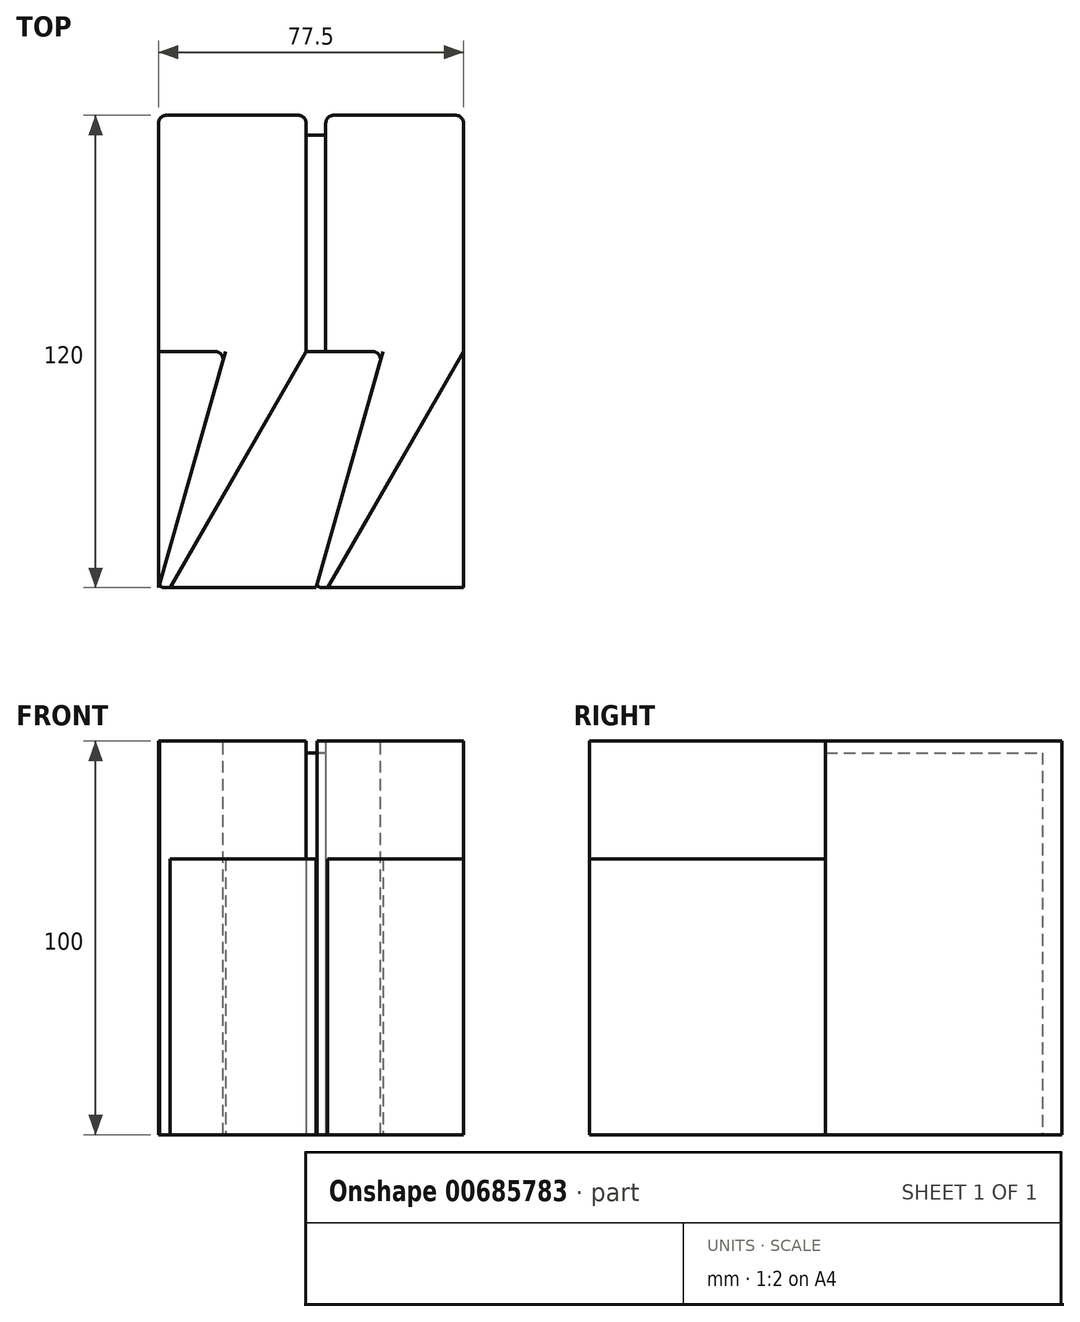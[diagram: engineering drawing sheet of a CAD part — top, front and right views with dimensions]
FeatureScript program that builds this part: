
annotation { "Feature Type Name" : "Feature", "Feature Type Description" : "" }
export const myFeature = defineFeature(function(context is Context, id is Id, definition is map)
    precondition{}
    {
        {
            var Q0;
            Q0=qCreatedBy(makeId("Top.planeOp"),FACE);
            var sketch = newSketch(context, id + "F0", { "sketchPlane" : qUnion([Q0])});
            skLineSegment(sketch, "E0.bottom", {"start": v(37.5, 60) * mm, "end": v(-40, 60) * mm});
            skLineSegment(sketch, "E0.top", {"start": v(37.5, -60) * mm, "end": v(-40, -60) * mm});
            skLineSegment(sketch, "E0.right", {"start": v(-40, 60) * mm, "end": v(-40, -60) * mm});
            skPoint(sketch, "E0.middle", {"position": v(0, 0) * mm});
            skLineSegment(sketch, "E1", {"start": v(-40, 0) * mm, "end": v(-23, 0) * mm});
            skLineSegment(sketch, "E2", {"start": v(-23, 0) * mm, "end": v(-40, -60) * mm});
            skLineSegment(sketch, "E3", {"start": v(17, 0) * mm, "end": v(0, -60) * mm});
            skLineSegment(sketch, "E4", {"start": v(0, -60) * mm, "end": v(3, -60) * mm});
            skLineSegment(sketch, "E5", {"start": v(3, -60) * mm, "end": v(0, -60) * mm});
            skLineSegment(sketch, "E6", {"start": v(-37, -60) * mm, "end": v(-40, -60) * mm});
            skPoint(sketch, "E7.end.orphan", {"position": v(30.1, 0) * mm});
            skPoint(sketch, "E8.start.orphan", {"position": v(-9.9, 0) * mm});
            skLineSegment(sketch, "E9", {"start": v(-37, -60) * mm, "end": v(-2.5, 0) * mm});
            skLineSegment(sketch, "E10", {"start": v(3, -60) * mm, "end": v(37.5, 0) * mm});
            skLineSegment(sketch, "E11", {"start": v(37.5, 0) * mm, "end": v(37.5, 60) * mm});
            skLineSegment(sketch, "E12", {"start": v(37.5, 0) * mm, "end": v(37.5, -60) * mm});
            skPoint(sketch, "E0.left.start.orphan", {"position": v(40, 60) * mm});
            skPoint(sketch, "E13.orphan", {"position": v(40, -60) * mm});
            skLineSegment(sketch, "E14", {"start": v(-2.5, 0) * mm, "end": v(17, 0) * mm});
            skLineSegment(sketch, "E15", {"start": v(-2.5, 0) * mm, "end": v(-2.5, 60) * mm});
            skLineSegment(sketch, "E16", {"start": v(2.5, 0) * mm, "end": v(2.5, 60) * mm});
            skSolve(sketch);
        }
        {
            var Q0;
            {var subQ3=sQuery(id+"F0.wireOp",EDGE,"E1");Q0=makeQuery(id+"F0.imprint","IMPRINT",FACE,{"disambiguationData":[TD([[makeQuery(id+"F0.imprint","IMPRINT",EDGE,{"derivedFrom":subQ3}),1.0]])]});}
            var Q1;
            {var subQ0=sQuery(id+"F0.wireOp",EDGE,"E3");Q1=makeQuery(id+"F0.imprint","IMPRINT",FACE,{"disambiguationData":[TD([[makeQuery(id+"F0.imprint","IMPRINT",EDGE,{"derivedFrom":subQ0}),1.0]])]});}
            extrude(context, id + "F1", {"entities" : qUnion([Q0, Q1]), "depth" : 100 * mm, "offsetDistance" : 25 * mm});
        }
        {
            var Q0;
            {var subQ2=sQuery(id+"F0.wireOp",EDGE,"E1");Q0=makeQuery(id+"F0.imprint","IMPRINT",FACE,{"disambiguationData":[TD([[makeQuery(id+"F0.imprint","IMPRINT",EDGE,{"derivedFrom":subQ2}),-1.0]])]});}
            var Q1;
            {var subQ3=sQuery(id+"F0.wireOp",EDGE,"E3");Q1=makeQuery(id+"F0.imprint","IMPRINT",FACE,{"disambiguationData":[TD([[makeQuery(id+"F0.imprint","IMPRINT",EDGE,{"derivedFrom":subQ3}),-1.0]])]});}
            var Q2;
            {var subQ2=sQuery(id+"F0.wireOp",EDGE,"E10");Q2=makeQuery(id+"F0.imprint","IMPRINT",FACE,{"disambiguationData":[TD([[makeQuery(id+"F0.imprint","IMPRINT",EDGE,{"derivedFrom":subQ2}),-1.0]])]});}
            extrude(context, id + "F2", {"entities" : qUnion([Q0, Q1, Q2]), "depth" : 70 * mm, "offsetDistance" : 25 * mm});
        }
        {
            var Q0;
            {var subQ0=sQuery(id+"F0.wireOp",EDGE,"E15");Q0=makeQuery(id+"F0.imprint","IMPRINT",FACE,{"disambiguationData":[TD([[makeQuery(id+"F0.imprint","IMPRINT",EDGE,{"derivedFrom":subQ0}),-1.0]])]});}
            extrude(context, id + "F3", {"entities" : qUnion([Q0]), "depth" : 97 * mm, "offsetDistance" : 25 * mm});
        }
        {
            var Q0;
            Q0=makeQuery(id+"F3.opExtrude","SWEPT_FACE",FACE,{"disambiguationData":[OSD([sQuery(id+"F0.wireOp",EDGE,"E0.bottom")])]});
            extrude(context, id + "F4", {"entities" : qUnion([Q0]), "operationType" : NewBodyOperationType.REMOVE, "oppositeDirection" : true, "depth" : 5 * mm, "offsetDistance" : 25 * mm});
        }
        {
            var Q0;
            Q0=makeQuery(id+"F1.opExtrude","SWEPT_EDGE",EDGE,{"disambiguationData":[OSD([sQuery(id+"F0.wireOp",EDGE,"E0.bottom"),sQuery(id+"F0.wireOp",EDGE,"E15")])]});
            fillet(context, id + "F5", {"entities" : qUnion([Q0]), "radius" : 2 * mm, "tangentPropagation" : true, "allowEdgeOverflow" : false});
        }
        {
            var Q0;
            Q0=makeQuery(id+"F1.opExtrude","SWEPT_EDGE",EDGE,{"disambiguationData":[OSD([sQuery(id+"F0.wireOp",EDGE,"E0.bottom"),sQuery(id+"F0.wireOp",EDGE,"E0.right")])]});
            fillet(context, id + "F6", {"entities" : qUnion([Q0]), "radius" : 2 * mm, "tangentPropagation" : true, "allowEdgeOverflow" : false});
        }
        {
            var Q0;
            Q0=makeQuery(id+"F1.opExtrude","SWEPT_EDGE",EDGE,{"disambiguationData":[OSD([sQuery(id+"F0.wireOp",EDGE,"E0.bottom"),sQuery(id+"F0.wireOp",EDGE,"E16")])]});
            var Q1;
            Q1=makeQuery(id+"F1.opExtrude","SWEPT_EDGE",EDGE,{"disambiguationData":[OSD([sQuery(id+"F0.wireOp",EDGE,"E0.bottom"),sQuery(id+"F0.wireOp",EDGE,"E11")])]});
            fillet(context, id + "F7", {"entities" : qUnion([Q0, Q1]), "radius" : 2 * mm, "tangentPropagation" : true, "allowEdgeOverflow" : false});
        }
        {
            var Q0;
            Q0=makeQuery(id+"F1.opExtrude","SWEPT_EDGE",EDGE,{"disambiguationData":[OSD([sQuery(id+"F0.wireOp",EDGE,"E1"),sQuery(id+"F0.wireOp",EDGE,"E2")])]});
            var Q1;
            Q1=makeQuery(id+"F1.opExtrude","SWEPT_EDGE",EDGE,{"disambiguationData":[OSD([sQuery(id+"F0.wireOp",EDGE,"E3"),sQuery(id+"F0.wireOp",EDGE,"E14")])]});
            fillet(context, id + "F8", {"entities" : qUnion([Q0, Q1]), "radius" : 2 * mm, "tangentPropagation" : true, "allowEdgeOverflow" : false});
        }
        {
            var Q0;
            Q0=makeQuery(id+"F1.opExtrude","SWEPT_EDGE",EDGE,{"disambiguationData":[OSD([sQuery(id+"F0.wireOp",EDGE,"E0.right"),sQuery(id+"F0.wireOp",EDGE,"E2"),sQuery(id+"F0.wireOp",EDGE,"E6")])]});
            fillet(context, id + "F9", {"entities" : qUnion([Q0]), "radius" : 1 * mm, "tangentPropagation" : true, "allowEdgeOverflow" : false});
        }
        {
            var Q0;
            Q0=makeQuery(id+"F1.opExtrude","SWEPT_EDGE",EDGE,{"disambiguationData":[OSD([sQuery(id+"F0.wireOp",EDGE,"E0.top"),sQuery(id+"F0.wireOp",EDGE,"E3"),sQuery(id+"F0.wireOp",EDGE,"E5")])]});
            fillet(context, id + "F10", {"entities" : qUnion([Q0]), "radius" : 1 * mm, "tangentPropagation" : true, "allowEdgeOverflow" : false});
        }
        {
            var Q0;
            Q0=makeQuery(id+"F1.opExtrude","SWEPT_EDGE",EDGE,{"disambiguationData":[OSD([sQuery(id+"F0.wireOp",EDGE,"E0.top"),sQuery(id+"F0.wireOp",EDGE,"E6"),sQuery(id+"F0.wireOp",EDGE,"E9")])]});
            var Q1;
            Q1=makeQuery(id+"F1.opExtrude","SWEPT_EDGE",EDGE,{"disambiguationData":[OSD([sQuery(id+"F0.wireOp",EDGE,"E0.top"),sQuery(id+"F0.wireOp",EDGE,"E5"),sQuery(id+"F0.wireOp",EDGE,"E10")])]});
            fillet(context, id + "F11", {"entities" : qUnion([Q0, Q1]), "radius" : 1 * mm, "tangentPropagation" : true, "allowEdgeOverflow" : false});
        }
    });
